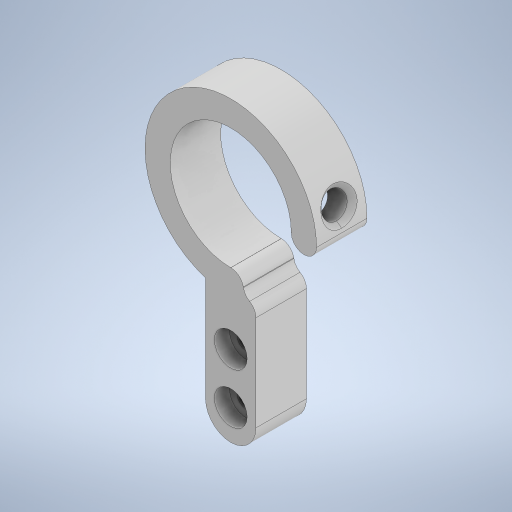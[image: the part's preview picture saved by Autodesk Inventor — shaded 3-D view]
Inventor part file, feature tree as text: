
AUTODESK INVENTOR PART (.ipt)
format: ipt  version: 2023.1 (Build 271208000, 208)  size: 328,192 bytes
history: native  units: mm
features: sketch x4, extrude x3, fillet x2, other x1, revolve x1, chamfer x1
ambient origin geometry x8: Origin, YZ Plane, XZ Plane, XY Plane, X Axis, Y Axis, Z Axis, Center Point
bodies: Body1 (feature_tree)
feature tree (12):
  other  "솔리드1"
  extrude  "돌출1"  Depth=10.0mm
  fillet  "모깎기1"  Radius=30.0mm
  revolve  "회전1"
  chamfer  "모따기1"  Distance=24.0mm
  extrude  "돌출2"  Depth=34.0mm
  fillet  "모깎기2"  Radius=10.0mm
  extrude  "돌출3"  Depth=2.5mm
  sketch  "스케치1"
  sketch  "스케치2"
  sketch  "스케치3"
  sketch  "스케치4"
